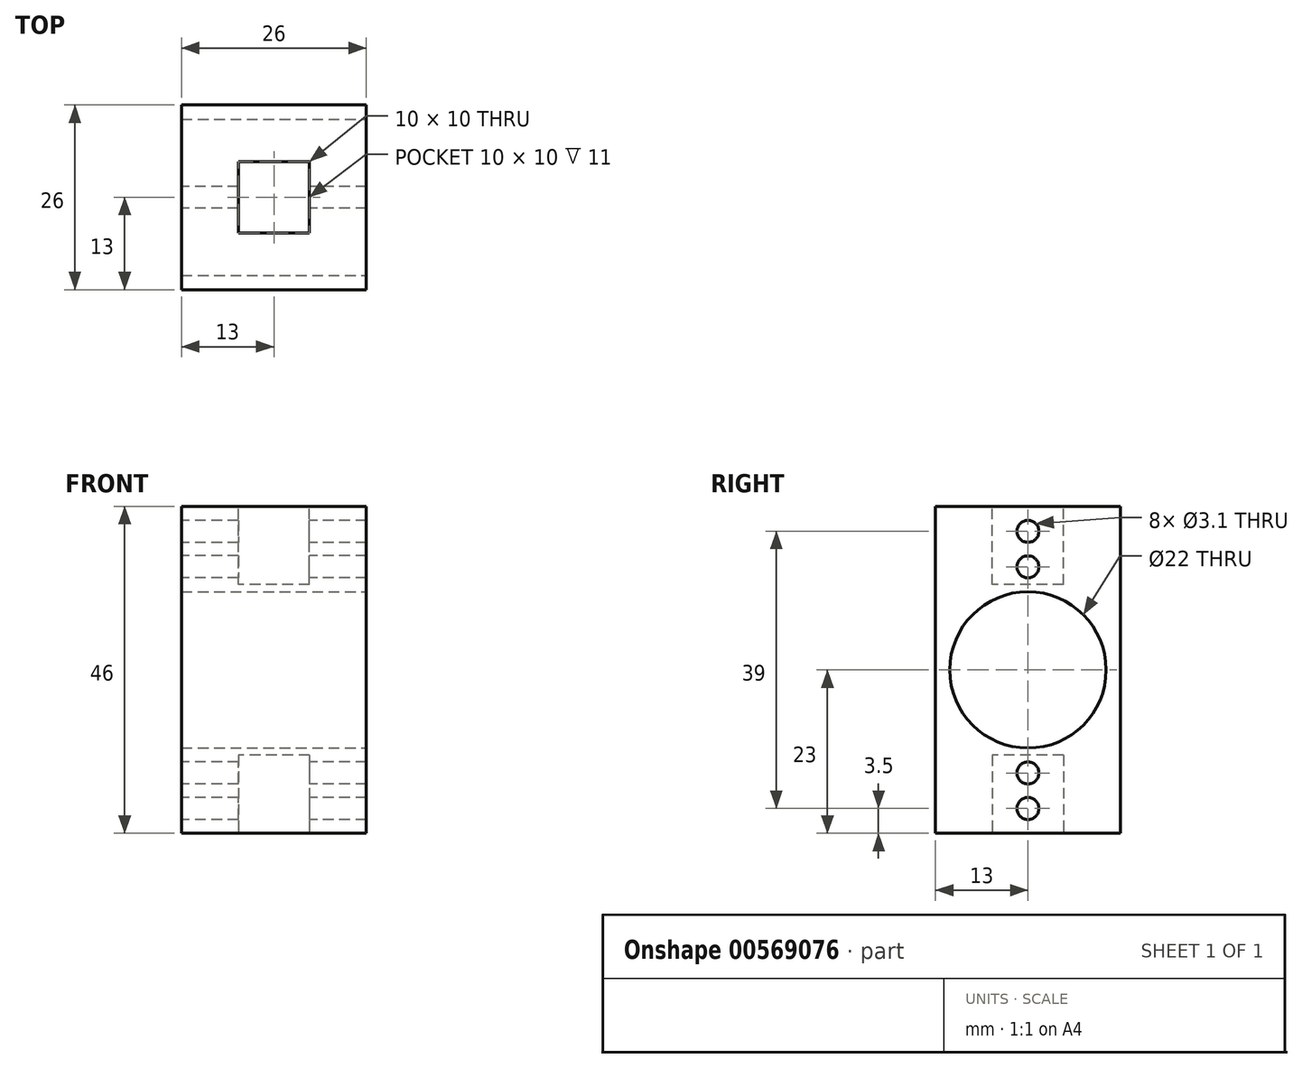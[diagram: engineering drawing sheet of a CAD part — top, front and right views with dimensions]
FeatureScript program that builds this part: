
annotation { "Feature Type Name" : "Feature", "Feature Type Description" : "" }
export const myFeature = defineFeature(function(context is Context, id is Id, definition is map)
    precondition{}
    {
        {
            var Q0;
            Q0=qCreatedBy(makeId("Front.planeOp"),FACE);
            var sketch = newSketch(context, id + "F0", { "sketchPlane" : qUnion([Q0])});
            skLineSegment(sketch, "E0", {"start": v(0, 0) * mm, "end": v(26, 0) * mm});
            skLineSegment(sketch, "E1", {"start": v(26, 0) * mm, "end": v(26, 46) * mm});
            skLineSegment(sketch, "E2", {"start": v(26, 46) * mm, "end": v(0, 46) * mm});
            skLineSegment(sketch, "E3", {"start": v(0, 46) * mm, "end": v(0, 0) * mm});
            skSolve(sketch);
        }
        {
            var Q0;
            Q0 = qSketchRegion(id + "F0", true);
            extrude(context, id + "F1", {"entities" : qUnion([Q0]), "depth" : 26 * mm, "offsetDistance" : 25 * mm});
        }
        {
            var Q0;
            Q0=makeQuery(id+"F1.opExtrude","SWEPT_FACE",FACE,{"disambiguationData":[OSD([sQuery(id+"F0.wireOp",EDGE,"E2")])]});
            var sketch = newSketch(context, id + "F2", { "sketchPlane" : qUnion([Q0])});
            skLineSegment(sketch, "E4", {"start": v(8, -8) * mm, "end": v(8, -18) * mm});
            skLineSegment(sketch, "E5", {"start": v(8, -18) * mm, "end": v(18, -18) * mm});
            skLineSegment(sketch, "E6", {"start": v(18, -18) * mm, "end": v(18, -8) * mm});
            skLineSegment(sketch, "E7", {"start": v(18, -8) * mm, "end": v(8, -8) * mm});
            skSolve(sketch);
        }
        {
            var Q0;
            Q0 = qSketchRegion(id + "F2", true);
            extrude(context, id + "F3", {"entities" : qUnion([Q0]), "operationType" : NewBodyOperationType.REMOVE, "oppositeDirection" : true, "depth" : 11 * mm, "offsetDistance" : 25 * mm});
        }
        {
            var Q0;
            Q0=makeQuery(id+"F1.opExtrude","SWEPT_FACE",FACE,{"disambiguationData":[OSD([sQuery(id+"F0.wireOp",EDGE,"E0")])]});
            var sketch = newSketch(context, id + "F4", { "sketchPlane" : qUnion([Q0])});
            skLineSegment(sketch, "E8", {"start": v(8, 8) * mm, "end": v(8, 18) * mm});
            skLineSegment(sketch, "E9", {"start": v(8, 18) * mm, "end": v(18, 18) * mm});
            skLineSegment(sketch, "E10", {"start": v(18, 18) * mm, "end": v(18, 8) * mm});
            skLineSegment(sketch, "E11", {"start": v(18, 8) * mm, "end": v(8, 8) * mm});
            skSolve(sketch);
        }
        {
            var Q0;
            Q0 = qSketchRegion(id + "F4", true);
            extrude(context, id + "F5", {"entities" : qUnion([Q0]), "operationType" : NewBodyOperationType.REMOVE, "oppositeDirection" : true, "depth" : 11 * mm, "offsetDistance" : 25 * mm});
        }
        {
            var Q0;
            Q0=makeQuery(id+"F1.opExtrude","SWEPT_FACE",FACE,{"disambiguationData":[OSD([sQuery(id+"F0.wireOp",EDGE,"E1")])]});
            var sketch = newSketch(context, id + "F6", { "sketchPlane" : qUnion([Q0])});
            skCircle(sketch, "E12", {"center": v(-13, 23) * mm, "radius": 11 * mm});
            skSolve(sketch);
        }
        {
            var Q0;
            Q0=makeQuery(id+"F1.opExtrude","SWEPT_FACE",FACE,{"disambiguationData":[OSD([sQuery(id+"F0.wireOp",EDGE,"E3")])]});
            var sketch = newSketch(context, id + "F7", { "sketchPlane" : qUnion([Q0])});
            skCircle(sketch, "E13", {"center": v(13, 8.5) * mm, "radius": 1.55 * mm});
            skCircle(sketch, "E14", {"center": v(13, 3.5) * mm, "radius": 1.55 * mm});
            skCircle(sketch, "E15", {"center": v(13, 42.5) * mm, "radius": 1.55 * mm});
            skCircle(sketch, "E16", {"center": v(13, 37.5) * mm, "radius": 1.55 * mm});
            skSolve(sketch);
        }
        {
            var Q0;
            Q0 = qSketchRegion(id + "F7", true);
            extrude(context, id + "F8", {"entities" : qUnion([Q0]), "operationType" : NewBodyOperationType.REMOVE, "oppositeDirection" : true, "depth" : 26 * mm, "offsetDistance" : 25 * mm});
        }
        {
            var Q0;
            Q0 = qSketchRegion(id + "F6", true);
            extrude(context, id + "F9", {"entities" : qUnion([Q0]), "operationType" : NewBodyOperationType.REMOVE, "oppositeDirection" : true, "depth" : 26 * mm, "offsetDistance" : 25 * mm});
        }
    });
